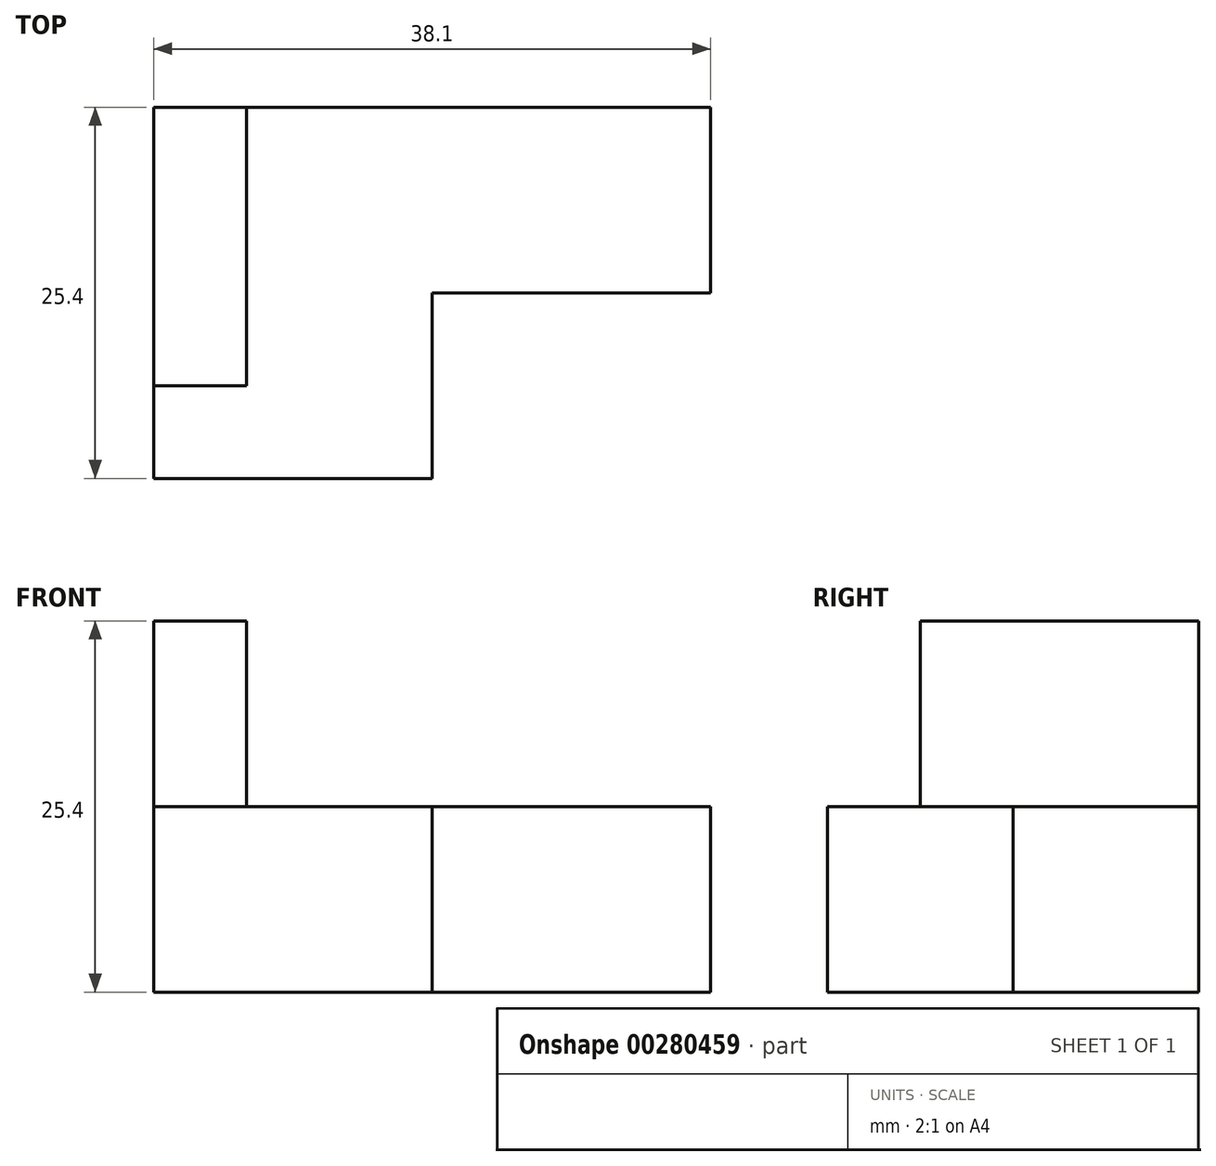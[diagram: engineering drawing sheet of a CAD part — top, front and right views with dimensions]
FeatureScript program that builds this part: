
annotation { "Feature Type Name" : "Feature", "Feature Type Description" : "" }
export const myFeature = defineFeature(function(context is Context, id is Id, definition is map)
    precondition{}
    {
        {
            var Q0;
            Q0=qCreatedBy(makeId("Top.planeOp"),FACE);
            var sketch = newSketch(context, id + "F0", { "sketchPlane" : qUnion([Q0])});
            skLineSegment(sketch, "E0.bottom", {"start": v(0, 0) * mm, "end": v(38.1, 0) * mm});
            skLineSegment(sketch, "E0.top", {"start": v(0, 25.4) * mm, "end": v(38.1, 25.4) * mm});
            skLineSegment(sketch, "E0.left", {"start": v(0, 0) * mm, "end": v(0, 25.4) * mm});
            skLineSegment(sketch, "E0.right", {"start": v(38.1, 0) * mm, "end": v(38.1, 25.4) * mm});
            skSolve(sketch);
        }
        {
            var Q0;
            Q0=makeQuery(id+"F0.imprint","IMPRINT",FACE,{"disambiguationData":[TD([[makeQuery(id+"F0.imprint","IMPRINT",EDGE,{"derivedFrom":sQuery(id+"F0.wireOp",EDGE,"E0.bottom")}),1.0]])]});
            extrude(context, id + "F1", {"entities" : qUnion([Q0]), "depth" : 12.7 * mm});
        }
        {
            var Q0;
            Q0=makeQuery(id+"F1.opExtrude","CAP_FACE",FACE,{"disambiguationData":[OSD([sQuery(id+"F0.wireOp",EDGE,"E0.bottom"),sQuery(id+"F0.wireOp",EDGE,"E0.top"),sQuery(id+"F0.wireOp",EDGE,"E0.left"),sQuery(id+"F0.wireOp",EDGE,"E0.right")])],"isStart":false});
            var sketch = newSketch(context, id + "F2", { "sketchPlane" : qUnion([Q0])});
            skLineSegment(sketch, "E1.bottom", {"start": v(38.1, 0) * mm, "end": v(19.05, 0) * mm});
            skLineSegment(sketch, "E1.top", {"start": v(38.1, 12.7) * mm, "end": v(19.05, 12.7) * mm});
            skLineSegment(sketch, "E1.left", {"start": v(38.1, 0) * mm, "end": v(38.1, 12.7) * mm});
            skLineSegment(sketch, "E1.right", {"start": v(19.05, 0) * mm, "end": v(19.05, 12.7) * mm});
            skSolve(sketch);
        }
        {
            var Q0;
            Q0=makeQuery(id+"F2.imprint","IMPRINT",FACE,{"disambiguationData":[TD([[makeQuery(id+"F2.imprint","IMPRINT",EDGE,{"derivedFrom":sQuery(id+"F2.wireOp",EDGE,"E1.bottom")}),1.0]])]});
            extrude(context, id + "F3", {"entities" : qUnion([Q0]), "operationType" : NewBodyOperationType.REMOVE, "endBound" : BoundingType.THROUGH_ALL, "oppositeDirection" : true, "depth" : 25.4 * mm});
        }
        {
            var Q0;
            Q0=makeQuery(id+"F1.opExtrude","CAP_FACE",FACE,{"disambiguationData":[OSD([sQuery(id+"F0.wireOp",EDGE,"E0.bottom"),sQuery(id+"F0.wireOp",EDGE,"E0.top"),sQuery(id+"F0.wireOp",EDGE,"E0.left"),sQuery(id+"F0.wireOp",EDGE,"E0.right")])],"isStart":false});
            var sketch = newSketch(context, id + "F4", { "sketchPlane" : qUnion([Q0])});
            skLineSegment(sketch, "E2.bottom", {"start": v(0, 25.4) * mm, "end": v(6.35, 25.4) * mm});
            skLineSegment(sketch, "E2.top", {"start": v(0, 6.35) * mm, "end": v(6.35, 6.35) * mm});
            skLineSegment(sketch, "E2.left", {"start": v(0, 25.4) * mm, "end": v(0, 6.35) * mm});
            skLineSegment(sketch, "E2.right", {"start": v(6.35, 25.4) * mm, "end": v(6.35, 6.35) * mm});
            skSolve(sketch);
        }
        {
            var Q0;
            Q0=makeQuery(id+"F4.imprint","IMPRINT",FACE,{"disambiguationData":[TD([[makeQuery(id+"F4.imprint","IMPRINT",EDGE,{"derivedFrom":sQuery(id+"F4.wireOp",EDGE,"E2.bottom")}),-1.0]])]});
            extrude(context, id + "F5", {"entities" : qUnion([Q0]), "operationType" : NewBodyOperationType.ADD, "depth" : 12.7 * mm});
        }
    });
